# Revit family: CADS_Vent-Axia_MechEquip_Fan_ESP_3Ph8P - SUPPLY
name_source: partatom
category: Mechanical Equipment
units: mm (PartAtom-declared; Revit-internal decimal feet)

## family parameters
Always vertical = Yes
Cut with Voids When Loaded = No
OmniClass Number = 23.75.00.00
OmniClass Title = Climate Control (HVAC)
Part Type = Normal
Room Calculation Point = No
Round Connector Dimension = Use Diameter
Shared = No
Work Plane-Based = No

## types (3) — shared parameters
AirflowRateRange = 0.0 L/s
AssemblyPlace = UNKNOWN
AssetType = FIXED
DurationUnit = Year
ExteriorInsulation = No
Fitting Type = Ignore
GrossWeight = 0.00 kg
HasProtectiveEarth = No
IfcExportAs = IfcFanType
IsExtendedWarranty = No
ManufacturerAddress = Fleming Way
Crawley 
RH10 9YX
Quantity = 1
RatedCurrent = 0 A
RatedVoltage = 0 V
Status = New
WarrantyGuarantor = Vent-Axia Limited
WorkingPressure = 0.0 Pa
zero-valued in all types: CADS_Index, CADS_Usage, Default Elevation, ExpectedServiceLife, NumberOfPoles

## per-type parameters (varying)
| type | A | E | G | ModelReference | NominalDiameter | NominalHeight | NominalLength | NominalWidth |
| T100_ESP100038 | 1170 mm  [stored 3.83858 ft] | 40 mm  [stored 0.131234 ft] | 20 mm  [stored 0.0656168 ft] | AXIAL PLATE FAN 1000DIA 3PH 8 POLE | 1000 mm  [stored 3.28084 ft] | 1170 mm  [stored 3.83858 ft] | 284 mm  [stored 0.931759 ft] | 1170 mm  [stored 3.83858 ft] |
| T100_ESP63038 | 805 mm  [stored 2.64108 ft] | 82 mm  [stored 0.269029 ft] | 20 mm  [stored 0.0656168 ft] | AXIAL PLATE FAN 630DIA 3PH 8 POLE | 630 mm  [stored 2.06693 ft] | 805 mm  [stored 2.64108 ft] | 143 mm | 805 mm  [stored 2.64108 ft] |
| T100_ESP80038 | 970 mm  [stored 3.18241 ft] | 34 mm | 17 mm | AXIAL PLATE FAN 800DIA 3PH 8 POLE | 800 mm  [stored 2.62467 ft] | 970 mm  [stored 3.18241 ft] | 244 mm  [stored 0.800525 ft] | 970 mm  [stored 3.18241 ft] |

note: column(s) folded — value = type name in every type: ModelNumber

note: [stored X ft] marks values corroborated as IEEE doubles in the binary element streams (Revit-internal decimal feet)

## geometry (parser evidence)
native form markers: Sweep x12
no freeform markers — native parametric forms only
